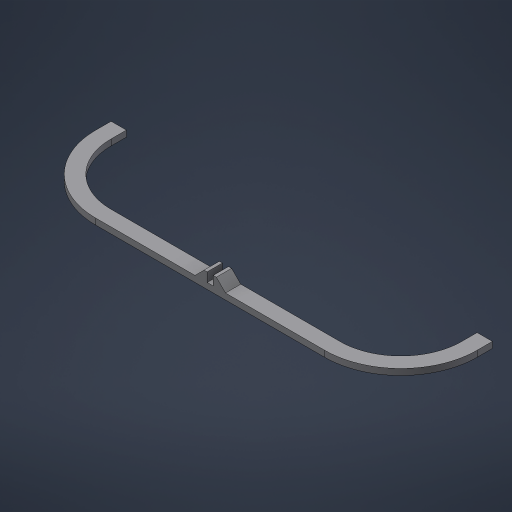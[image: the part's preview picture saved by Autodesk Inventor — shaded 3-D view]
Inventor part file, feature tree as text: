
AUTODESK INVENTOR PART (.ipt)
format: ipt  version: 2023.5 (Build 275446000, 446)  size: 207,872 bytes
history: native  units: mm
features: sketch x2, extrude x2, mirror x1, chamfer x1
ambient origin geometry x8: Origin, YZ Plane, XZ Plane, XY Plane, X Axis, Y Axis, Z Axis, Center Point
bodies: Volumenkörper1 (feature_tree)
feature tree (6):
  sketch  "Skizze1"  dims[d0=5.0mm d2=30.0mm]
  extrude  "Extrusion1"  Depth=30.0mm
  extrude  "Extrusion2"  Depth=120.0mm
  mirror  "Spiegeln1"
  chamfer  "Fase1"  Distance=10.0mm
  sketch  "Skizze2"  dims[d3=25.0mm d4=120.0mm d6=10.0mm d7=2.0mm d8=2.0mm d9=0.0mm d10=5.0mm d11=0.0mm d12=3.0mm d13=2.0mm d14=45.0deg d15=5.0mm d16=3.0mm d17=60.0mm d19=25.0mm]
